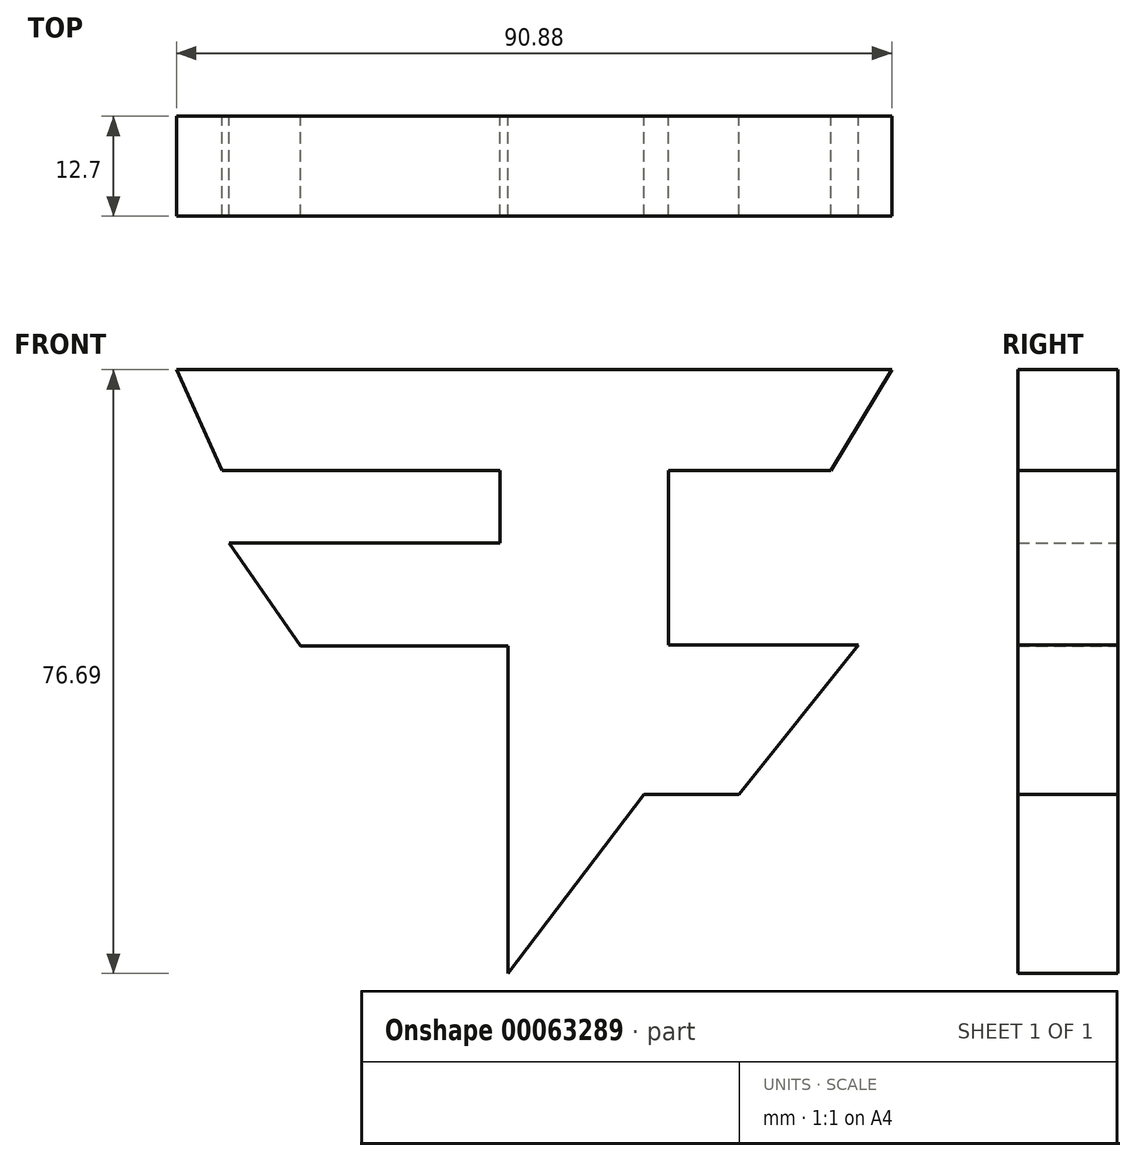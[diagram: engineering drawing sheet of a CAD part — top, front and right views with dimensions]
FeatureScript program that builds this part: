
annotation { "Feature Type Name" : "Feature", "Feature Type Description" : "" }
export const myFeature = defineFeature(function(context is Context, id is Id, definition is map)
    precondition{}
    {
        {
            var Q0;
            Q0=qCreatedBy(makeId("Front.planeOp"),FACE);
            var sketch = newSketch(context, id + "F0", { "sketchPlane" : qUnion([Q0])});
            skLineSegment(sketch, "E0", {"start": v(-32.99, -26.59) * mm, "end": v(-32.99, 15.02) * mm});
            skLineSegment(sketch, "E1", {"start": v(-32.99, 15.02) * mm, "end": v(-59.33, 15.02) * mm});
            skLineSegment(sketch, "E2", {"start": v(-59.33, 15.02) * mm, "end": v(-68.44, 28.07) * mm});
            skLineSegment(sketch, "E3", {"start": v(-68.44, 28.07) * mm, "end": v(-33.97, 28.07) * mm});
            skLineSegment(sketch, "E4", {"start": v(-33.97, 28.07) * mm, "end": v(-33.97, 37.29) * mm});
            skLineSegment(sketch, "E5", {"start": v(-33.97, 37.29) * mm, "end": v(-69.28, 37.29) * mm});
            skLineSegment(sketch, "E6", {"start": v(-69.28, 37.29) * mm, "end": v(-75.11, 50.1) * mm});
            skLineSegment(sketch, "E7", {"start": v(-75.11, 50.1) * mm, "end": v(15.77, 50.1) * mm});
            skLineSegment(sketch, "E8", {"start": v(15.77, 50.1) * mm, "end": v(8, 37.29) * mm});
            skLineSegment(sketch, "E9", {"start": v(8, 37.29) * mm, "end": v(-12.58, 37.29) * mm});
            skLineSegment(sketch, "E10", {"start": v(-12.58, 37.29) * mm, "end": v(-12.58, 15.15) * mm});
            skLineSegment(sketch, "E11", {"start": v(-12.58, 15.15) * mm, "end": v(11.5, 15.15) * mm});
            skLineSegment(sketch, "E12", {"start": v(11.5, 15.15) * mm, "end": v(-3.64, -3.88) * mm});
            skLineSegment(sketch, "E13", {"start": v(-3.64, -3.88) * mm, "end": v(-15.69, -3.88) * mm});
            skLineSegment(sketch, "E14", {"start": v(-15.69, -3.88) * mm, "end": v(-32.99, -26.59) * mm});
            skSolve(sketch);
        }
        {
            var Q0;
            Q0=makeQuery(id+"F0.imprint","IMPRINT",FACE,{"disambiguationData":[TD([[makeQuery(id+"F0.imprint","IMPRINT",EDGE,{"derivedFrom":sQuery(id+"F0.wireOp",EDGE,"E0")}),-1.0]])]});
            extrude(context, id + "F1", {"entities" : qUnion([Q0]), "depth" : 12.7 * mm});
        }
    });
